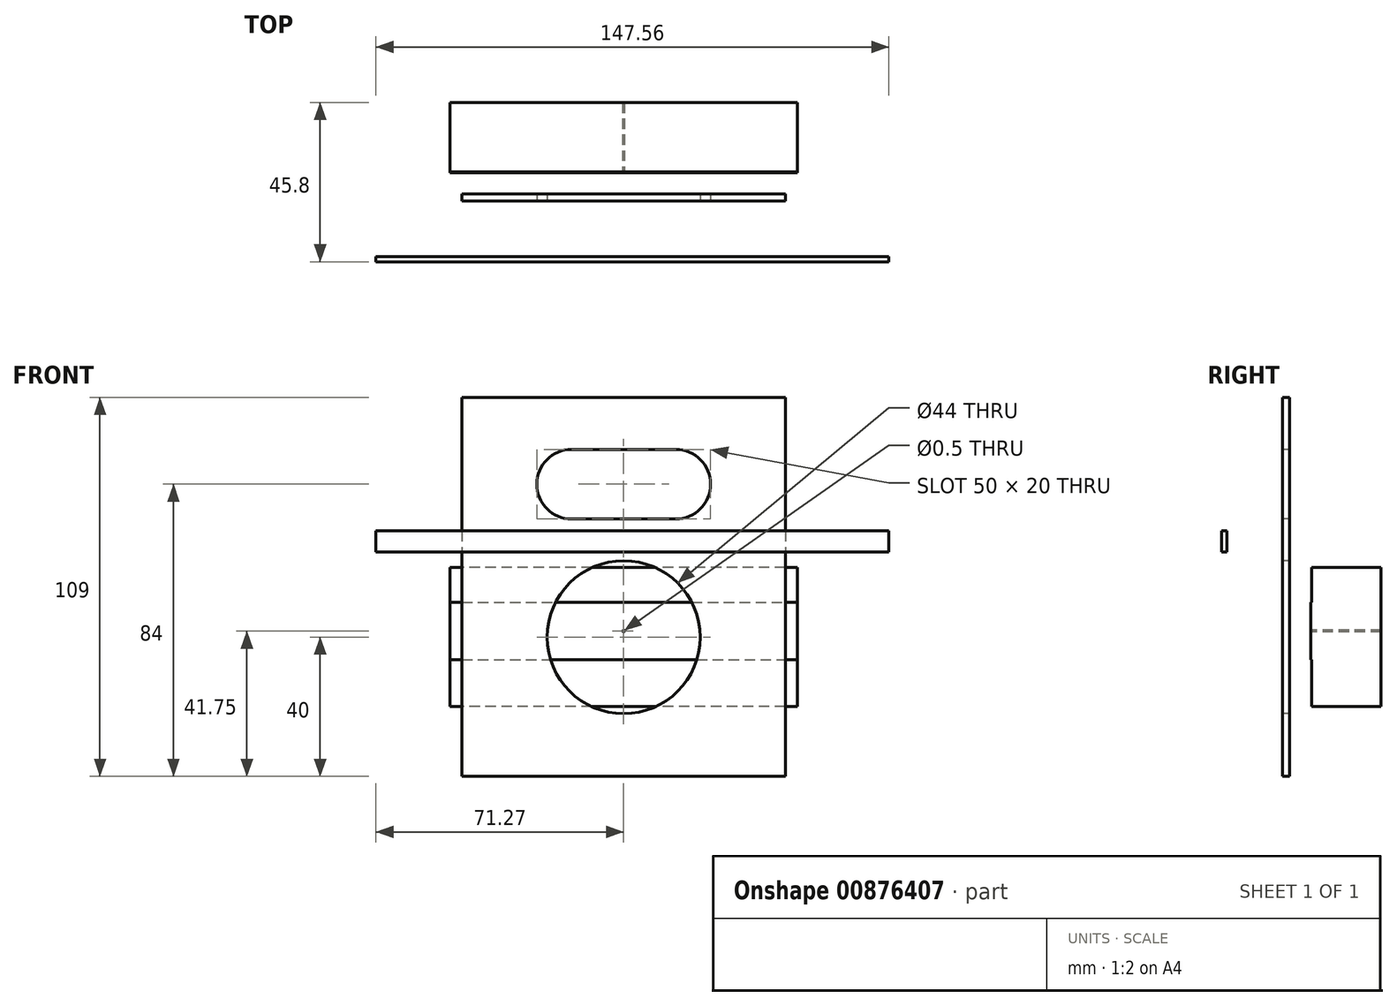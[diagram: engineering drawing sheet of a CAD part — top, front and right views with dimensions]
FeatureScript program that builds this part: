
annotation { "Feature Type Name" : "Feature", "Feature Type Description" : "" }
export const myFeature = defineFeature(function(context is Context, id is Id, definition is map)
    precondition{}
    {
        {
            var Q0;
            Q0=qCreatedBy(makeId("Front.planeOp"),FACE);
            var sketch = newSketch(context, id + "F0", { "sketchPlane" : qUnion([Q0])});
            skLineSegment(sketch, "E0.bottom", {"start": v(50, -20) * mm, "end": v(-50, -20) * mm});
            skLineSegment(sketch, "E0.top", {"start": v(50, 20) * mm, "end": v(-50, 20) * mm});
            skLineSegment(sketch, "E0.left", {"start": v(50, -20) * mm, "end": v(50, 20) * mm});
            skLineSegment(sketch, "E0.right", {"start": v(-50, -20) * mm, "end": v(-50, 20) * mm});
            skPoint(sketch, "E0.middle", {"position": v(0, 0) * mm});
            skLineSegment(sketch, "E1.bottom", {"start": v(-50, 10) * mm, "end": v(50, 10) * mm});
            skLineSegment(sketch, "E1.top", {"start": v(-50, -6.5) * mm, "end": v(50, -6.5) * mm});
            skLineSegment(sketch, "E1.left", {"start": v(-50, 10) * mm, "end": v(-50, -6.5) * mm});
            skLineSegment(sketch, "E1.right", {"start": v(50, 10) * mm, "end": v(50, -6.5) * mm});
            skLineSegment(sketch, "E2", {"start": v(0, 10) * mm, "end": v(0, -6.5) * mm, "construction": true});
            skPoint(sketch, "E3", {"position": v(0, 1.75) * mm});
            skLineSegment(sketch, "E4", {"start": v(-9.4, 1.75) * mm, "end": v(7.83, 1.75) * mm, "construction": true});
            skCircle(sketch, "E5", {"center": v(0, 1.75) * mm, "radius": 0.25 * mm});
            skSolve(sketch);
        }
        {
            var Q0;
            {var subQ0=sQuery(id+"F0.wireOp",EDGE,"E0.top");Q0=makeQuery(id+"F0.imprint","IMPRINT",FACE,{"disambiguationData":[TD([[makeQuery(id+"F0.imprint","IMPRINT",EDGE,{"derivedFrom":subQ0}),1.0]])]});}
            var Q1;
            {var subQ2=sQuery(id+"F0.wireOp",EDGE,"E1.bottom");Q1=makeQuery(id+"F0.imprint","IMPRINT",FACE,{"disambiguationData":[TD([[makeQuery(id+"F0.imprint","IMPRINT",EDGE,{"derivedFrom":subQ2}),-1.0]])]});}
            var Q2;
            {var subQ0=sQuery(id+"F0.wireOp",EDGE,"E0.bottom");Q2=makeQuery(id+"F0.imprint","IMPRINT",FACE,{"disambiguationData":[TD([[makeQuery(id+"F0.imprint","IMPRINT",EDGE,{"derivedFrom":subQ0}),-1.0]])]});}
            extrude(context, id + "F1", {"entities" : qUnion([Q0, Q1, Q2]), "oppositeDirection" : true, "depth" : 20 * mm, "offsetDistance" : 25 * mm});
        }
        {
            var Q0;
            {var subQ2=sQuery(id+"F0.wireOp",EDGE,"E1.bottom");Q0=makeQuery(id+"F0.imprint","IMPRINT",FACE,{"disambiguationData":[TD([[makeQuery(id+"F0.imprint","IMPRINT",EDGE,{"derivedFrom":subQ2}),-1.0]])]});}
            extrude(context, id + "F2", {"entities" : qUnion([Q0]), "operationType" : NewBodyOperationType.ADD, "depth" : 0.2 * mm, "offsetDistance" : 25 * mm});
        }
        {
            var Q0;
            {var subQ0=sQuery(id+"F0.wireOp",EDGE,"E0.top");Q0=makeQuery(id+"F0.imprint","IMPRINT",FACE,{"disambiguationData":[TD([[makeQuery(id+"F0.imprint","IMPRINT",EDGE,{"derivedFrom":subQ0}),1.0]])]});}
            cPlane(context, id + "F3", {"entities" : qUnion([Q0]), "cplaneType" : CPlaneType.OFFSET, "offset" : 8.3 * mm, "width" : 150 * mm, "height" : 150 * mm});
        }
        {
            var Q0;
            Q0=qCreatedBy(id+"F3.planeOp",FACE);
            var sketch = newSketch(context, id + "F4", { "sketchPlane" : qUnion([Q0])});
            skLineSegment(sketch, "E6.bottom", {"start": v(-46.5, 69) * mm, "end": v(46.5, 69) * mm});
            skLineSegment(sketch, "E6.top", {"start": v(-46.5, -40) * mm, "end": v(46.5, -40) * mm});
            skLineSegment(sketch, "E6.left", {"start": v(-46.5, 69) * mm, "end": v(-46.5, -40) * mm});
            skLineSegment(sketch, "E6.right", {"start": v(46.5, 69) * mm, "end": v(46.5, -40) * mm});
            skCircle(sketch, "E7", {"center": v(0, 0) * mm, "radius": 22 * mm});
            skArc(sketch, "E8", {"start": v(-15, 54) * mm, "mid": v(-25, 44) * mm, "end": v(-15, 34) * mm});
            skArc(sketch, "E9", {"start": v(15, 34) * mm, "mid": v(25, 44) * mm, "end": v(15, 54) * mm});
            skLineSegment(sketch, "E10", {"start": v(-15, 54) * mm, "end": v(15, 54) * mm});
            skLineSegment(sketch, "E11", {"start": v(-15, 34) * mm, "end": v(15, 34) * mm});
            skPoint(sketch, "E12", {"position": v(0, 44) * mm});
            skSolve(sketch);
        }
        {
            var Q0;
            Q0=makeQuery(id+"F4.imprint","IMPRINT",FACE,{"disambiguationData":[TD([[makeQuery(id+"F4.imprint","IMPRINT",EDGE,{"derivedFrom":sQuery(id+"F4.wireOp",EDGE,"E6.bottom")}),-1.0]])]});
            extrude(context, id + "F5", {"entities" : qUnion([Q0]), "oppositeDirection" : true, "depth" : 2 * mm, "offsetDistance" : 25 * mm});
        }
        {
            var Q0;
            Q0=makeQuery(id+"F5.opExtrude","CAP_FACE",FACE,{"disambiguationData":[OSD([sQuery(id+"F4.wireOp",EDGE,"E6.bottom"),sQuery(id+"F4.wireOp",EDGE,"E6.top"),sQuery(id+"F4.wireOp",EDGE,"E6.left"),sQuery(id+"F4.wireOp",EDGE,"E6.right"),sQuery(id+"F4.wireOp",EDGE,"E7"),sQuery(id+"F4.wireOp",EDGE,"E8"),sQuery(id+"F4.wireOp",EDGE,"E9"),sQuery(id+"F4.wireOp",EDGE,"E10"),sQuery(id+"F4.wireOp",EDGE,"E11")])],"isStart":true});
            cPlane(context, id + "F6", {"entities" : qUnion([Q0]), "cplaneType" : CPlaneType.OFFSET, "offset" : 16 * mm, "width" : 150 * mm, "height" : 150 * mm});
        }
        {
            var Q0;
            Q0=qCreatedBy(id+"F6.planeOp",FACE);
            var sketch = newSketch(context, id + "F7", { "sketchPlane" : qUnion([Q0])});
            skLineSegment(sketch, "E13.bottom", {"start": v(-71.27, 30.56) * mm, "end": v(76.29, 30.56) * mm});
            skLineSegment(sketch, "E13.top", {"start": v(-71.27, 24.56) * mm, "end": v(76.29, 24.56) * mm});
            skLineSegment(sketch, "E13.left", {"start": v(-71.27, 30.56) * mm, "end": v(-71.27, 24.56) * mm});
            skLineSegment(sketch, "E13.right", {"start": v(76.29, 30.56) * mm, "end": v(76.29, 24.56) * mm});
            skSolve(sketch);
        }
        {
            var Q0;
            Q0=makeQuery(id+"F7.imprint","IMPRINT",FACE,{"disambiguationData":[TD([[makeQuery(id+"F7.imprint","IMPRINT",EDGE,{"derivedFrom":sQuery(id+"F7.wireOp",EDGE,"E13.bottom")}),-1.0]])]});
            extrude(context, id + "F8", {"entities" : qUnion([Q0]), "depth" : 1.5 * mm, "offsetDistance" : 25 * mm});
        }
    });
